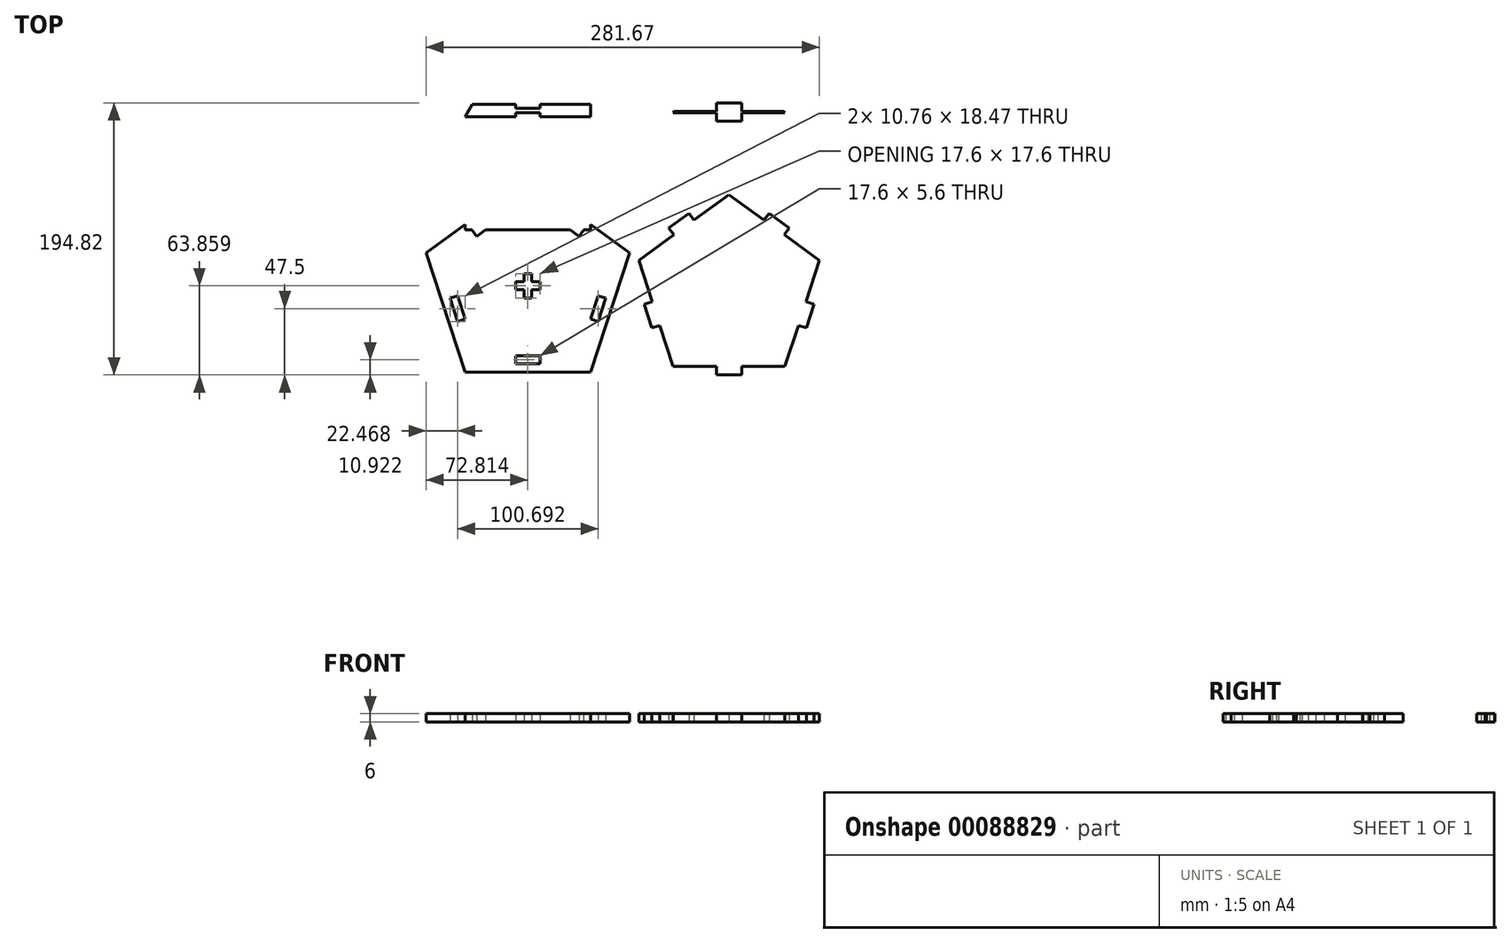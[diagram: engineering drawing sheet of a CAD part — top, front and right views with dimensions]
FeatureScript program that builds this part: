
annotation { "Feature Type Name" : "Feature", "Feature Type Description" : "" }
export const myFeature = defineFeature(function(context is Context, id is Id, definition is map)
    precondition{}
    {
        {
            assignVariable(context, id + "F0", {"name" : "material_thickness", "anyValue" : 6});
        }
        {
            var Q0;
            Q0=qCreatedBy(makeId("Top.planeOp"),FACE);
            var sketch = newSketch(context, id + "F1", { "sketchPlane" : qUnion([Q0])});
            skLineSegment(sketch, "E0.bottom", {"start": v(-28.98, -124.92) * mm, "end": v(-46.98, -124.92) * mm, "construction": true});
            skLineSegment(sketch, "E0.top", {"start": v(-28.98, -130.92) * mm, "end": v(-46.98, -130.92) * mm, "construction": true});
            skLineSegment(sketch, "E0.left", {"start": v(-28.98, -124.92) * mm, "end": v(-28.98, -130.92) * mm, "construction": true});
            skLineSegment(sketch, "E0.right", {"start": v(-46.98, -124.92) * mm, "end": v(-46.98, -130.92) * mm, "construction": true});
            skPoint(sketch, "E0.middle", {"position": v(-37.98, -127.92) * mm});
            skLineSegment(sketch, "E1.0", {"start": v(-75.3, 107.56) * mm, "end": v(-30.3, 29.62) * mm});
            skLineSegment(sketch, "E1.1", {"start": v(-30.3, 29.62) * mm, "end": v(-120.3, 29.62) * mm});
            skLineSegment(sketch, "E1.2", {"start": v(-120.3, 29.62) * mm, "end": v(-75.3, 107.56) * mm});
            skPoint(sketch, "E2", {"position": v(-75.3, 55.6) * mm});
            skCircle(sketch, "E3", {"center": v(-75.3, 55.6) * mm, "radius": 51.96 * mm, "construction": true});
            skLineSegment(sketch, "E4.0", {"start": v(-30.3, 38.6) * mm, "end": v(-30.3, -51.4) * mm});
            skLineSegment(sketch, "E4.1", {"start": v(-30.3, -51.4) * mm, "end": v(-120.3, -51.4) * mm});
            skLineSegment(sketch, "E4.2", {"start": v(-120.3, -51.4) * mm, "end": v(-120.3, 38.6) * mm});
            skLineSegment(sketch, "E4.3", {"start": v(-120.3, 38.6) * mm, "end": v(-30.3, 38.6) * mm});
            skCircle(sketch, "E5.cCircle", {"center": v(-75.3, -91.36) * mm, "radius": 61.94 * mm, "construction": true});
            skLineSegment(sketch, "E5.0", {"start": v(-2.48, -67.7) * mm, "end": v(-30.3, -153.3) * mm});
            skLineSegment(sketch, "E5.1", {"start": v(-30.3, -153.3) * mm, "end": v(-120.3, -153.3) * mm});
            skLineSegment(sketch, "E5.2", {"start": v(-120.3, -153.3) * mm, "end": v(-148.1, -67.7) * mm});
            skLineSegment(sketch, "E5.3", {"start": v(-148.1, -67.7) * mm, "end": v(-75.3, -14.8) * mm});
            skLineSegment(sketch, "E5.4", {"start": v(-75.3, -14.8) * mm, "end": v(-2.48, -67.7) * mm});
            skPoint(sketch, "E5.0.midPoint", {"position": v(-16.4, -110.5) * mm});
            skLineSegment(sketch, "E6", {"start": v(-75.3, 128.3) * mm, "end": v(-75.3, -178.57) * mm, "construction": true});
            skCircle(sketch, "E7", {"center": v(-75.3, -6.4) * mm, "radius": 63.64 * mm, "construction": true});
            skLineSegment(sketch, "E8.bottom", {"start": v(-66.3, -147.3) * mm, "end": v(-84.3, -147.3) * mm, "construction": true});
            skLineSegment(sketch, "E8.top", {"start": v(-66.3, -141.3) * mm, "end": v(-84.3, -141.3) * mm, "construction": true});
            skLineSegment(sketch, "E8.left", {"start": v(-66.3, -147.3) * mm, "end": v(-66.3, -141.3) * mm, "construction": true});
            skLineSegment(sketch, "E8.right", {"start": v(-84.3, -147.3) * mm, "end": v(-84.3, -141.3) * mm, "construction": true});
            skPoint(sketch, "E8.middle", {"position": v(-75.3, -144.3) * mm});
            skLineSegment(sketch, "E9", {"start": v(-75.3, -147.3) * mm, "end": v(-75.3, -153.3) * mm, "construction": true});
            skLineSegment(sketch, "E10.bottom", {"start": v(-66.3, -88.36) * mm, "end": v(-72.3, -88.36) * mm, "construction": true});
            skLineSegment(sketch, "E10.top", {"start": v(-66.3, -94.36) * mm, "end": v(-72.3, -94.36) * mm, "construction": true});
            skLineSegment(sketch, "E10.left", {"start": v(-66.3, -88.36) * mm, "end": v(-66.3, -94.36) * mm, "construction": true});
            skLineSegment(sketch, "E10.right", {"start": v(-84.3, -88.36) * mm, "end": v(-84.3, -94.36) * mm, "construction": true});
            skLineSegment(sketch, "E11.bottom", {"start": v(-72.3, -100.36) * mm, "end": v(-78.3, -100.36) * mm, "construction": true});
            skLineSegment(sketch, "E11.top", {"start": v(-72.3, -82.36) * mm, "end": v(-78.3, -82.36) * mm, "construction": true});
            skLineSegment(sketch, "E11.left", {"start": v(-72.3, -100.36) * mm, "end": v(-72.3, -94.36) * mm, "construction": true});
            skLineSegment(sketch, "E11.right", {"start": v(-78.3, -100.36) * mm, "end": v(-78.3, -94.36) * mm, "construction": true});
            skLineSegment(sketch, "E12.trimOffspring", {"start": v(-78.3, -88.36) * mm, "end": v(-84.3, -88.36) * mm, "construction": true});
            skLineSegment(sketch, "E13.trimOffspring", {"start": v(-72.3, -88.36) * mm, "end": v(-72.3, -82.36) * mm, "construction": true});
            skLineSegment(sketch, "E14.trimOffspring", {"start": v(-78.3, -94.36) * mm, "end": v(-84.3, -94.36) * mm, "construction": true});
            skLineSegment(sketch, "E15.trimOffspring", {"start": v(-78.3, -88.36) * mm, "end": v(-78.3, -82.36) * mm, "construction": true});
            skLineSegment(sketch, "E16.0", {"start": v(-84.1, -147.1) * mm, "end": v(-84.1, -141.5) * mm});
            skLineSegment(sketch, "E16.1", {"start": v(-66.5, -147.1) * mm, "end": v(-84.1, -147.1) * mm});
            skLineSegment(sketch, "E16.2", {"start": v(-66.5, -147.1) * mm, "end": v(-66.5, -141.5) * mm});
            skLineSegment(sketch, "E16.3", {"start": v(-66.5, -141.5) * mm, "end": v(-84.1, -141.5) * mm});
            skLineSegment(sketch, "E17.1.0", {"start": v(-19.57, -100.22) * mm, "end": v(-25, -116.95) * mm});
            skLineSegment(sketch, "E17.1.1", {"start": v(-19.57, -100.22) * mm, "end": v(-24.9, -98.49) * mm});
            skLineSegment(sketch, "E17.1.2", {"start": v(-24.9, -98.49) * mm, "end": v(-30.33, -115.22) * mm});
            skLineSegment(sketch, "E17.1.3", {"start": v(-25, -116.95) * mm, "end": v(-30.33, -115.22) * mm});
            skLineSegment(sketch, "E17.2.0", {"start": v(-49.65, -41.1) * mm, "end": v(-35.42, -51.44) * mm});
            skLineSegment(sketch, "E17.2.1", {"start": v(-49.65, -41.1) * mm, "end": v(-52.95, -45.63) * mm});
            skLineSegment(sketch, "E17.2.2", {"start": v(-52.95, -45.63) * mm, "end": v(-38.7, -55.97) * mm});
            skLineSegment(sketch, "E17.2.3", {"start": v(-35.42, -51.44) * mm, "end": v(-38.7, -55.97) * mm});
            skLineSegment(sketch, "E17.3.0", {"start": v(-115.18, -51.44) * mm, "end": v(-100.94, -41.1) * mm});
            skLineSegment(sketch, "E17.3.1", {"start": v(-115.18, -51.44) * mm, "end": v(-111.89, -55.97) * mm});
            skLineSegment(sketch, "E17.3.2", {"start": v(-111.89, -55.97) * mm, "end": v(-97.65, -45.63) * mm});
            skLineSegment(sketch, "E17.3.3", {"start": v(-100.94, -41.1) * mm, "end": v(-97.65, -45.63) * mm});
            skLineSegment(sketch, "E17.4.0", {"start": v(-125.59, -116.95) * mm, "end": v(-131.02, -100.22) * mm});
            skLineSegment(sketch, "E17.4.1", {"start": v(-125.59, -116.95) * mm, "end": v(-120.26, -115.22) * mm});
            skLineSegment(sketch, "E17.4.2", {"start": v(-120.26, -115.22) * mm, "end": v(-125.7, -98.49) * mm});
            skLineSegment(sketch, "E17.4.3", {"start": v(-131.02, -100.22) * mm, "end": v(-125.7, -98.49) * mm});
            skLineSegment(sketch, "E18.0", {"start": v(-66.5, -88.56) * mm, "end": v(-72.5, -88.56) * mm});
            skLineSegment(sketch, "E18.1", {"start": v(-84.1, -88.56) * mm, "end": v(-84.1, -94.16) * mm});
            skLineSegment(sketch, "E18.2", {"start": v(-78.1, -88.56) * mm, "end": v(-84.1, -88.56) * mm});
            skLineSegment(sketch, "E18.3", {"start": v(-78.1, -88.56) * mm, "end": v(-78.1, -82.56) * mm});
            skLineSegment(sketch, "E18.4", {"start": v(-72.5, -82.56) * mm, "end": v(-78.1, -82.56) * mm});
            skLineSegment(sketch, "E18.5", {"start": v(-78.1, -94.16) * mm, "end": v(-84.1, -94.16) * mm});
            skLineSegment(sketch, "E18.6", {"start": v(-72.5, -88.56) * mm, "end": v(-72.5, -82.56) * mm});
            skLineSegment(sketch, "E18.7", {"start": v(-78.1, -100.16) * mm, "end": v(-78.1, -94.16) * mm});
            skLineSegment(sketch, "E18.8", {"start": v(-72.5, -100.16) * mm, "end": v(-78.1, -100.16) * mm});
            skLineSegment(sketch, "E18.9", {"start": v(-72.5, -100.16) * mm, "end": v(-72.5, -94.16) * mm});
            skLineSegment(sketch, "E18.10", {"start": v(-66.5, -94.16) * mm, "end": v(-72.5, -94.16) * mm});
            skLineSegment(sketch, "E18.11", {"start": v(-66.5, -88.56) * mm, "end": v(-66.5, -94.16) * mm});
            skLineSegment(sketch, "E19", {"start": v(-84.3, -91.36) * mm, "end": v(-66.3, -91.36) * mm, "construction": true});
            skLineSegment(sketch, "E20", {"start": v(-75.3, -82.36) * mm, "end": v(-75.3, -100.36) * mm, "construction": true});
            skLineSegment(sketch, "E21.bottom", {"start": v(-78.3, -88.36) * mm, "end": v(-72.3, -88.36) * mm, "construction": true});
            skLineSegment(sketch, "E21.top", {"start": v(-78.3, -94.36) * mm, "end": v(-72.3, -94.36) * mm, "construction": true});
            skLineSegment(sketch, "E21.left", {"start": v(-78.3, -88.36) * mm, "end": v(-78.3, -94.36) * mm, "construction": true});
            skLineSegment(sketch, "E21.right", {"start": v(-72.3, -88.36) * mm, "end": v(-72.3, -94.36) * mm, "construction": true});
            skLineSegment(sketch, "E22.bottom", {"start": v(-66.3, -39.4) * mm, "end": v(-84.3, -39.4) * mm, "construction": true});
            skLineSegment(sketch, "E22.top", {"start": v(-66.3, -45.4) * mm, "end": v(-84.3, -45.4) * mm, "construction": true});
            skLineSegment(sketch, "E22.left", {"start": v(-66.3, -39.4) * mm, "end": v(-66.3, -45.4) * mm, "construction": true});
            skLineSegment(sketch, "E22.right", {"start": v(-84.3, -39.4) * mm, "end": v(-84.3, -45.4) * mm, "construction": true});
            skPoint(sketch, "E22.middle", {"position": v(-75.3, -42.4) * mm});
            skLineSegment(sketch, "E23", {"start": v(-75.3, -45.4) * mm, "end": v(-75.3, -51.4) * mm, "construction": true});
            skLineSegment(sketch, "E24.0", {"start": v(-84.1, -39.6) * mm, "end": v(-84.1, -45.2) * mm});
            skLineSegment(sketch, "E24.1", {"start": v(-66.5, -39.6) * mm, "end": v(-84.1, -39.6) * mm});
            skLineSegment(sketch, "E24.2", {"start": v(-66.5, -39.6) * mm, "end": v(-66.5, -45.2) * mm});
            skLineSegment(sketch, "E24.3", {"start": v(-66.5, -45.2) * mm, "end": v(-84.1, -45.2) * mm});
            skLineSegment(sketch, "E25.1.0", {"start": v(-42.1, 2.4) * mm, "end": v(-36.5, 2.4) * mm});
            skLineSegment(sketch, "E25.1.1", {"start": v(-36.5, 2.4) * mm, "end": v(-36.5, -15.2) * mm});
            skLineSegment(sketch, "E25.1.2", {"start": v(-42.1, 2.4) * mm, "end": v(-42.1, -15.2) * mm});
            skLineSegment(sketch, "E25.1.3", {"start": v(-42.1, -15.2) * mm, "end": v(-36.5, -15.2) * mm});
            skLineSegment(sketch, "E25.2.0", {"start": v(-84.1, 26.8) * mm, "end": v(-84.1, 32.4) * mm});
            skLineSegment(sketch, "E25.2.1", {"start": v(-84.1, 32.4) * mm, "end": v(-66.5, 32.4) * mm});
            skLineSegment(sketch, "E25.2.2", {"start": v(-84.1, 26.8) * mm, "end": v(-66.5, 26.8) * mm});
            skLineSegment(sketch, "E25.2.3", {"start": v(-66.5, 26.8) * mm, "end": v(-66.5, 32.4) * mm});
            skLineSegment(sketch, "E25.3.0", {"start": v(-108.5, -15.2) * mm, "end": v(-114.1, -15.2) * mm});
            skLineSegment(sketch, "E25.3.1", {"start": v(-114.1, -15.2) * mm, "end": v(-114.1, 2.4) * mm});
            skLineSegment(sketch, "E25.3.2", {"start": v(-108.5, -15.2) * mm, "end": v(-108.5, 2.4) * mm});
            skLineSegment(sketch, "E25.3.3", {"start": v(-108.5, 2.4) * mm, "end": v(-114.1, 2.4) * mm});
            skLineSegment(sketch, "E26.bottom", {"start": v(-66.3, -3.4) * mm, "end": v(-84.3, -3.4) * mm, "construction": true});
            skLineSegment(sketch, "E26.top", {"start": v(-66.3, -9.4) * mm, "end": v(-84.3, -9.4) * mm, "construction": true});
            skLineSegment(sketch, "E26.left", {"start": v(-66.3, -3.4) * mm, "end": v(-66.3, -9.4) * mm, "construction": true});
            skLineSegment(sketch, "E26.right", {"start": v(-84.3, -3.4) * mm, "end": v(-84.3, -9.4) * mm, "construction": true});
            skLineSegment(sketch, "E27.bottom", {"start": v(-72.3, -15.2) * mm, "end": v(-78.3, -15.2) * mm});
            skLineSegment(sketch, "E27.top", {"start": v(-72.3, 2.4) * mm, "end": v(-78.3, 2.4) * mm});
            skLineSegment(sketch, "E27.left", {"start": v(-72.3, -15.2) * mm, "end": v(-72.3, -9.2) * mm});
            skLineSegment(sketch, "E27.right", {"start": v(-78.3, -15.2) * mm, "end": v(-78.3, -9.2) * mm});
            skLineSegment(sketch, "E28.0", {"start": v(-72.1, 2.6) * mm, "end": v(-78.5, 2.6) * mm, "construction": true});
            skLineSegment(sketch, "E28.1", {"start": v(-72.1, -15.4) * mm, "end": v(-72.1, 2.6) * mm, "construction": true});
            skLineSegment(sketch, "E28.2", {"start": v(-72.1, -15.4) * mm, "end": v(-78.5, -15.4) * mm, "construction": true});
            skLineSegment(sketch, "E28.3", {"start": v(-78.5, -15.4) * mm, "end": v(-78.5, 2.6) * mm, "construction": true});
            skLineSegment(sketch, "E29.0", {"start": v(-66.5, -9.2) * mm, "end": v(-72.3, -9.2) * mm});
            skLineSegment(sketch, "E29.1", {"start": v(-66.5, -3.6) * mm, "end": v(-66.5, -9.2) * mm});
            skLineSegment(sketch, "E29.2", {"start": v(-66.5, -3.6) * mm, "end": v(-72.3, -3.6) * mm});
            skLineSegment(sketch, "E29.3", {"start": v(-84.1, -3.6) * mm, "end": v(-84.1, -9.2) * mm});
            skLineSegment(sketch, "E30.trimOffspring", {"start": v(-72.3, -3.6) * mm, "end": v(-72.3, 2.4) * mm});
            skLineSegment(sketch, "E31.trimOffspring", {"start": v(-78.3, -3.6) * mm, "end": v(-84.1, -3.6) * mm});
            skLineSegment(sketch, "E32.trimOffspring", {"start": v(-78.3, -3.6) * mm, "end": v(-78.3, 2.4) * mm});
            skLineSegment(sketch, "E33.trimOffspring", {"start": v(-78.3, -9.2) * mm, "end": v(-84.1, -9.2) * mm});
            skLineSegment(sketch, "E34", {"start": v(-75.3, 2.6) * mm, "end": v(-75.3, -15.4) * mm, "construction": true});
            skLineSegment(sketch, "E35.bottom", {"start": v(-66.3, 35.62) * mm, "end": v(-84.3, 35.62) * mm, "construction": true});
            skLineSegment(sketch, "E35.top", {"start": v(-66.3, 41.62) * mm, "end": v(-84.3, 41.62) * mm, "construction": true});
            skLineSegment(sketch, "E35.left", {"start": v(-66.3, 35.62) * mm, "end": v(-66.3, 41.62) * mm, "construction": true});
            skLineSegment(sketch, "E35.right", {"start": v(-84.3, 35.62) * mm, "end": v(-84.3, 41.62) * mm, "construction": true});
            skPoint(sketch, "E35.middle", {"position": v(-75.3, 38.62) * mm});
            skLineSegment(sketch, "E36", {"start": v(-75.3, 35.62) * mm, "end": v(-75.3, 29.62) * mm, "construction": true});
            skLineSegment(sketch, "E37.0", {"start": v(-66.5, 41.42) * mm, "end": v(-84.1, 41.42) * mm});
            skLineSegment(sketch, "E37.1", {"start": v(-66.5, 35.82) * mm, "end": v(-66.5, 41.42) * mm});
            skLineSegment(sketch, "E37.2", {"start": v(-66.5, 35.82) * mm, "end": v(-84.1, 35.82) * mm});
            skLineSegment(sketch, "E37.3", {"start": v(-84.1, 35.82) * mm, "end": v(-84.1, 41.42) * mm});
            skLineSegment(sketch, "E38.1.0", {"start": v(-67.41, 70.3) * mm, "end": v(-58.61, 55.07) * mm});
            skLineSegment(sketch, "E38.1.1", {"start": v(-62.57, 73.1) * mm, "end": v(-67.41, 70.3) * mm});
            skLineSegment(sketch, "E38.1.2", {"start": v(-62.57, 73.1) * mm, "end": v(-53.77, 57.87) * mm});
            skLineSegment(sketch, "E38.1.3", {"start": v(-53.77, 57.87) * mm, "end": v(-58.61, 55.07) * mm});
            skLineSegment(sketch, "E38.2.0", {"start": v(-91.98, 55.07) * mm, "end": v(-83.18, 70.3) * mm});
            skLineSegment(sketch, "E38.2.1", {"start": v(-96.83, 57.87) * mm, "end": v(-91.98, 55.07) * mm});
            skLineSegment(sketch, "E38.2.2", {"start": v(-96.83, 57.87) * mm, "end": v(-88.03, 73.1) * mm});
            skLineSegment(sketch, "E38.2.3", {"start": v(-88.03, 73.1) * mm, "end": v(-83.18, 70.3) * mm});
            skLineSegment(sketch, "E39", {"start": v(68.84, 182.03) * mm, "end": v(68.84, -156.42) * mm, "construction": true});
            skLineSegment(sketch, "E40", {"start": v(-75.3, 55.6) * mm, "end": v(68.84, 55.6) * mm, "construction": true});
            skCircle(sketch, "E41.cCircle", {"center": v(68.84, 55.6) * mm, "radius": 23.1 * mm, "construction": true});
            skLineSegment(sketch, "E41.0", {"start": v(108.84, 32.5) * mm, "end": v(28.84, 32.5) * mm, "construction": true});
            skLineSegment(sketch, "E41.1", {"start": v(28.84, 32.5) * mm, "end": v(68.84, 101.79) * mm, "construction": true});
            skLineSegment(sketch, "E41.2", {"start": v(68.84, 101.79) * mm, "end": v(108.84, 32.5) * mm, "construction": true});
            skPoint(sketch, "E41.0.midPoint", {"position": v(68.84, 32.5) * mm});
            skLineSegment(sketch, "E42.bottom", {"start": v(77.84, 32.5) * mm, "end": v(59.84, 32.5) * mm, "construction": true});
            skLineSegment(sketch, "E42.top", {"start": v(77.84, 26.5) * mm, "end": v(59.84, 26.5) * mm});
            skLineSegment(sketch, "E42.left", {"start": v(77.84, 32.5) * mm, "end": v(77.84, 26.5) * mm});
            skLineSegment(sketch, "E42.right", {"start": v(59.84, 32.5) * mm, "end": v(59.84, 26.5) * mm});
            skLineSegment(sketch, "E43.1.0", {"start": v(84.34, 74.94) * mm, "end": v(89.53, 77.94) * mm});
            skLineSegment(sketch, "E43.1.1", {"start": v(89.53, 77.94) * mm, "end": v(98.53, 62.35) * mm});
            skLineSegment(sketch, "E43.1.2", {"start": v(93.34, 59.35) * mm, "end": v(98.53, 62.35) * mm});
            skLineSegment(sketch, "E43.2.0", {"start": v(44.34, 59.35) * mm, "end": v(39.14, 62.35) * mm});
            skLineSegment(sketch, "E43.2.1", {"start": v(39.14, 62.35) * mm, "end": v(48.14, 77.94) * mm});
            skLineSegment(sketch, "E43.2.2", {"start": v(53.34, 74.94) * mm, "end": v(48.14, 77.94) * mm});
            skLineSegment(sketch, "E44", {"start": v(93.34, 59.35) * mm, "end": v(108.84, 32.5) * mm});
            skLineSegment(sketch, "E45", {"start": v(77.84, 32.5) * mm, "end": v(108.84, 32.5) * mm});
            skLineSegment(sketch, "E46", {"start": v(84.34, 74.94) * mm, "end": v(68.84, 101.79) * mm});
            skLineSegment(sketch, "E47", {"start": v(68.84, 101.79) * mm, "end": v(53.34, 74.94) * mm});
            skLineSegment(sketch, "E48", {"start": v(44.34, 59.35) * mm, "end": v(28.84, 32.5) * mm});
            skLineSegment(sketch, "E49", {"start": v(59.84, 32.5) * mm, "end": v(28.84, 32.5) * mm});
            skLineSegment(sketch, "E50", {"start": v(-75.3, -6.4) * mm, "end": v(68.84, -6.4) * mm, "construction": true});
            skLineSegment(sketch, "E51.bottom", {"start": v(108.84, -46.4) * mm, "end": v(28.84, -46.4) * mm, "construction": true});
            skLineSegment(sketch, "E51.top", {"start": v(108.84, 33.6) * mm, "end": v(28.84, 33.6) * mm, "construction": true});
            skLineSegment(sketch, "E51.left", {"start": v(108.84, -46.4) * mm, "end": v(108.84, 33.6) * mm, "construction": true});
            skLineSegment(sketch, "E51.right", {"start": v(28.84, -46.4) * mm, "end": v(28.84, 33.6) * mm, "construction": true});
            skPoint(sketch, "E51.middle", {"position": v(68.84, -6.4) * mm});
            skLineSegment(sketch, "E52.bottom", {"start": v(77.84, -52.4) * mm, "end": v(59.84, -52.4) * mm});
            skLineSegment(sketch, "E52.top", {"start": v(77.84, -46.4) * mm, "end": v(59.84, -46.4) * mm, "construction": true});
            skLineSegment(sketch, "E52.left", {"start": v(77.84, -52.4) * mm, "end": v(77.84, -46.4) * mm});
            skLineSegment(sketch, "E52.right", {"start": v(59.84, -52.4) * mm, "end": v(59.84, -46.4) * mm});
            skPoint(sketch, "E52.middle", {"position": v(68.84, -46.4) * mm});
            skLineSegment(sketch, "E53.1.0", {"start": v(114.84, 2.6) * mm, "end": v(114.84, -15.4) * mm});
            skLineSegment(sketch, "E53.1.1", {"start": v(114.84, 2.6) * mm, "end": v(108.84, 2.6) * mm});
            skLineSegment(sketch, "E53.1.2", {"start": v(114.84, -15.4) * mm, "end": v(108.84, -15.4) * mm});
            skLineSegment(sketch, "E53.2.0", {"start": v(59.84, 39.6) * mm, "end": v(77.84, 39.6) * mm});
            skLineSegment(sketch, "E53.2.1", {"start": v(59.84, 39.6) * mm, "end": v(59.84, 33.6) * mm});
            skLineSegment(sketch, "E53.2.2", {"start": v(77.84, 39.6) * mm, "end": v(77.84, 33.6) * mm});
            skLineSegment(sketch, "E53.3.0", {"start": v(22.84, -15.4) * mm, "end": v(22.84, 2.6) * mm});
            skLineSegment(sketch, "E53.3.1", {"start": v(22.84, -15.4) * mm, "end": v(28.84, -15.4) * mm});
            skLineSegment(sketch, "E53.3.2", {"start": v(22.84, 2.6) * mm, "end": v(28.84, 2.6) * mm});
            skLineSegment(sketch, "E54", {"start": v(77.84, -46.4) * mm, "end": v(108.84, -46.4) * mm});
            skLineSegment(sketch, "E55", {"start": v(108.84, 2.6) * mm, "end": v(108.84, 33.6) * mm});
            skLineSegment(sketch, "E56", {"start": v(77.84, 33.6) * mm, "end": v(108.84, 33.6) * mm});
            skLineSegment(sketch, "E57", {"start": v(59.84, 33.6) * mm, "end": v(28.84, 33.6) * mm});
            skLineSegment(sketch, "E58", {"start": v(28.84, 33.6) * mm, "end": v(28.84, 2.6) * mm});
            skLineSegment(sketch, "E59", {"start": v(28.84, -15.4) * mm, "end": v(28.84, -46.4) * mm});
            skLineSegment(sketch, "E60", {"start": v(28.84, -46.4) * mm, "end": v(59.84, -46.4) * mm});
            skLineSegment(sketch, "E61", {"start": v(108.84, -46.4) * mm, "end": v(108.84, -15.4) * mm});
            skLineSegment(sketch, "E62", {"start": v(-75.3, -91.36) * mm, "end": v(68.84, -94.16) * mm, "construction": true});
            skCircle(sketch, "E63.cCircle", {"center": v(68.84, -94.16) * mm, "radius": 55.06 * mm, "construction": true});
            skLineSegment(sketch, "E63.0", {"start": v(133.56, -73.13) * mm, "end": v(108.84, -149.22) * mm, "construction": true});
            skLineSegment(sketch, "E63.1", {"start": v(108.84, -149.22) * mm, "end": v(28.84, -149.22) * mm, "construction": true});
            skLineSegment(sketch, "E63.2", {"start": v(28.84, -149.22) * mm, "end": v(4.11, -73.13) * mm, "construction": true});
            skLineSegment(sketch, "E63.3", {"start": v(4.11, -73.13) * mm, "end": v(68.84, -26.1) * mm, "construction": true});
            skLineSegment(sketch, "E63.4", {"start": v(68.84, -26.1) * mm, "end": v(133.56, -73.13) * mm, "construction": true});
            skPoint(sketch, "E63.0.midPoint", {"position": v(121.2, -111.17) * mm});
            skLineSegment(sketch, "E64.bottom", {"start": v(77.84, -155.22) * mm, "end": v(59.84, -155.22) * mm});
            skLineSegment(sketch, "E64.top", {"start": v(77.84, -149.22) * mm, "end": v(59.84, -149.22) * mm, "construction": true});
            skLineSegment(sketch, "E64.left", {"start": v(77.84, -155.22) * mm, "end": v(77.84, -149.22) * mm});
            skLineSegment(sketch, "E64.right", {"start": v(59.84, -155.22) * mm, "end": v(59.84, -149.22) * mm});
            skPoint(sketch, "E65", {"position": v(68.84, -149.22) * mm});
            skLineSegment(sketch, "E66.1.0", {"start": v(129.68, -104.47) * mm, "end": v(124.12, -121.59) * mm});
            skLineSegment(sketch, "E66.1.1", {"start": v(129.68, -104.47) * mm, "end": v(123.98, -102.61) * mm});
            skLineSegment(sketch, "E66.1.2", {"start": v(124.12, -121.59) * mm, "end": v(118.42, -119.73) * mm});
            skLineSegment(sketch, "E66.2.0", {"start": v(97.44, -39.48) * mm, "end": v(112, -50.06) * mm});
            skLineSegment(sketch, "E66.2.1", {"start": v(97.44, -39.48) * mm, "end": v(93.92, -44.33) * mm});
            skLineSegment(sketch, "E66.2.2", {"start": v(112, -50.06) * mm, "end": v(108.48, -54.91) * mm});
            skLineSegment(sketch, "E66.3.0", {"start": v(25.67, -50.06) * mm, "end": v(40.23, -39.48) * mm});
            skLineSegment(sketch, "E66.3.1", {"start": v(25.67, -50.06) * mm, "end": v(29.2, -54.91) * mm});
            skLineSegment(sketch, "E66.3.2", {"start": v(40.23, -39.48) * mm, "end": v(43.76, -44.33) * mm});
            skLineSegment(sketch, "E66.4.0", {"start": v(13.55, -121.59) * mm, "end": v(7.99, -104.47) * mm});
            skLineSegment(sketch, "E66.4.1", {"start": v(13.55, -121.59) * mm, "end": v(19.26, -119.73) * mm});
            skLineSegment(sketch, "E66.4.2", {"start": v(7.99, -104.47) * mm, "end": v(13.7, -102.61) * mm});
            skLineSegment(sketch, "E67", {"start": v(77.84, -149.22) * mm, "end": v(108.84, -149.22) * mm});
            skLineSegment(sketch, "E68", {"start": v(108.84, -149.22) * mm, "end": v(118.42, -119.73) * mm});
            skLineSegment(sketch, "E69", {"start": v(123.98, -102.61) * mm, "end": v(133.56, -73.13) * mm});
            skLineSegment(sketch, "E70", {"start": v(133.56, -73.13) * mm, "end": v(108.48, -54.91) * mm});
            skLineSegment(sketch, "E71", {"start": v(93.92, -44.33) * mm, "end": v(68.84, -26.1) * mm});
            skLineSegment(sketch, "E72", {"start": v(68.84, -26.1) * mm, "end": v(43.76, -44.33) * mm});
            skLineSegment(sketch, "E73", {"start": v(29.2, -54.91) * mm, "end": v(4.11, -73.13) * mm});
            skLineSegment(sketch, "E74", {"start": v(4.11, -73.13) * mm, "end": v(13.7, -102.61) * mm});
            skLineSegment(sketch, "E75", {"start": v(19.26, -119.73) * mm, "end": v(28.84, -149.22) * mm});
            skLineSegment(sketch, "E76", {"start": v(59.84, -149.22) * mm, "end": v(28.84, -149.22) * mm});
            skSolve(sketch);
        }
        {
            var Q0;
            {var subQ3=sQuery(id+"F1.wireOp",EDGE,"E5.0");Q0=makeQuery(id+"F1.imprint","IMPRINT",FACE,{"disambiguationData":[TD([[makeQuery(id+"F1.imprint","IMPRINT",EDGE,{"derivedFrom":subQ3}),-1.0]])]});}
            var Q1;
            Q1=makeQuery(id+"F1.imprint","IMPRINT",FACE,{"disambiguationData":[TD([[makeQuery(id+"F1.imprint","IMPRINT",EDGE,{"derivedFrom":sQuery(id+"F1.wireOp",EDGE,"E4.0")}),-1.0]])]});
            var Q2;
            Q2=makeQuery(id+"F1.imprint","IMPRINT",FACE,{"disambiguationData":[TD([[makeQuery(id+"F1.imprint","IMPRINT",EDGE,{"derivedFrom":sQuery(id+"F1.wireOp",EDGE,"E1.0")}),-1.0]])]});
            var Q3;
            Q3=makeQuery(id+"F1.imprint","IMPRINT",FACE,{"disambiguationData":[TD([[makeQuery(id+"F1.imprint","IMPRINT",EDGE,{"derivedFrom":sQuery(id+"F1.wireOp",EDGE,"E42.top")}),-1.0]])]});
            var Q4;
            Q4=makeQuery(id+"F1.imprint","IMPRINT",FACE,{"disambiguationData":[TD([[makeQuery(id+"F1.imprint","IMPRINT",EDGE,{"derivedFrom":sQuery(id+"F1.wireOp",EDGE,"E52.bottom")}),-1.0]])]});
            var Q5;
            Q5=makeQuery(id+"F1.imprint","IMPRINT",FACE,{"disambiguationData":[TD([[makeQuery(id+"F1.imprint","IMPRINT",EDGE,{"derivedFrom":sQuery(id+"F1.wireOp",EDGE,"E64.bottom")}),-1.0]])]});
            extrude(context, id + "F2", {"entities" : qUnion([Q0, Q1, Q2, Q3, Q4, Q5]), "depth" : (getVariable(context, 'material_thickness')) * mm});
        }
    });
